# Revit family: ARGO-1200-xx-xx_V1.0_Non-Hosted_R16
name_source: partatom
category: Lighting Fixtures
revit_build: Autodesk Revit 2016 (Build: 20150220_1215(x64)
units: mm (PartAtom-declared; Revit-internal decimal feet)

## family parameters
Always vertical = Yes
Cut with Voids When Loaded = No
Light Source = Yes
OmniClass Number = 23.80.70.00
OmniClass Title = Lighting
Part Type = Normal
Room Calculation Point = No
Round Connector Dimension = Use Diameter
Shared = No
Work Plane-Based = No

## types (4) — shared parameters
Color Filter = 16777215
Construction = Polycarbonate Base and Captive Stainless Steel Clips (SS301)
Diffuser = Polycarbonate Diffuser
Dimensions (L x W x H) = 1265mm x 127mm x 88mm
Dimming Lamp Color Temperature Shift = <None>
Emit Shape Visible in Rendering = No
Emit from Rectangle Length = 1219 mm
Emit from Rectangle Width = 610 mm
IK Rating = IK08
IP Rating = IP65
Lamp = Dual LED strip module, 3,000K warm white, 5,700K cool white, 50,000h life [L70/B50 Ta 40°C], Ra>80
Manufacturer = Clevertronics
Mounting = Surface mount
Operating Temperature = 0˚C to 40˚C
Operating Voltage = 240V AC; 50Hz
Tilt Angle = 90.00°

## per-type parameters (varying)
| type | AS2293 Classification | Alternative Part Number | Battery | Battery Type | Charging Method | Emergency Lumen Output | LED Driver | MIC Number | Operating Mode | Photometric Web File | Power Factor | Product Description | Replacement Battery | Replacement Driver | Replacement Emergency Driver | Supply Current | Testing System | Total Lumen Output | Weight |
| ARGO-1200 |  | F4WB |  |  |  |  | LED Driver – 40w Stallion, SP | AUB04620360001 |  | ll22303A_ARGO-1200(LM-79,4000K,Hi).ies | 0.95 (HO), 0.9 (LO) | 240V Argonaut Quantum 1200mm Weatherproof Batten, Switchable Colour & Output |  | 1330083 LED Driver - 40w Stallion, SP |  | 180mA +/- 20mA |  | 3729lm (@3000K, HO), 4318lm (@4000K, HO), 4014lm (@5700K, HO), 2219lm (@3000K, LO), 2365lm (@4000K, LO), 2301lm (@5700K, LO) | 2.3 kg |
| ARGO-1200-SEN |  | F4WB-MS-HL |  |  |  |  | LED Driver – Merytek MLC65C | AUB04620370001 |  | ll22339a_ARGO-1200-SEN(LM-79,4000K).ies | 0.85 | 240V Argonaut Quantum 1200mm Weatherproof Batten Batten with Microwave Sensor (Hi/Lo) and
Switchable Colour
Switchable Colour |  | 1330079 LED HL Driver - MLC65C-P8 |  | 190mA +/- 20mA |  | 3684lm (@3000K), 4060lm (@4000K), 3732 (@5700K) | 2.4 kg |
| ARGO-1200-EM | C0=D40 C90=D25 | A4WB | 3.2V 3000mAh | Lithium Iron Phosphate | Intelligent current limited constant voltage | 302.5 lm | LED Driver – 40w Stallion, SP | AUB03520100001 | Sustained | ll22462A_ARGO-1200-EM(2-hr_Photometry).ies | 0.95 (HO), 0.9 (LO) | Economy Argonaut Quantum 1200mm Weatherproof Emergency Batten, Switchable Colour & Output | 1560150 BATT:LiFePO4 3.2V 3.0Ah 70mm lead,noBRKT | 1330083 LED Driver - 40w Stallion, SP | ELIFE-X-LI-CKIT-2LED-SLNP Lifelight, Control Only,2LED,3.0Ah,325mA | 180mA +/- 20mA | N/A - Manual test switch | 3729lm (@3000K, HO), 4256lm (@4000K, HO), 4014lm (@5700K, HO), 2219lm (@3000K, LO), 2365lm (@4000K, LO), 2301lm (@5700K, LO), | 2.6 kg |
| ARGO-1200-EM-SEN | C0=D40 C90=D25 | A4WB-MS-HL | 3.2V 3000mAh | Lithium Iron Phosphate | Intelligent current limited constant voltage | 305.5 lm | LED Driver – Merytek MLC65C | AUB03520110001 | Sustained | ll22464a_ARGO-1200-EM-SEN(2-hr_Photometry).ies | 0.85 | Economy Argonaut Quantum 1200mm Weatherproof Emergency Batten with Microwave Sensor
(Hi/Lo) and Switchable Colour
Switchable Colour
Switchable Colour | 1560150 BATT:LiFePO4 3.2V 3.0Ah 70mm lead,noBRKT | 1330079 LED HL Driver - MLC65C-P8 | ELIFE-X-LI-CKIT-2LED-SLNP Lifelight, Control Only,2LED,3.0Ah,325mA | 190mA +/- 20mA | N/A - Manual test switch | 3684lm (@3000K), 4060lm (@4000K), 3732 (@5700K) | 2.7 kg |

note: column(s) folded — value = type name in every type: Model

## geometry (parser evidence)
native form markers: Sweep x2
no freeform markers — native parametric forms only
